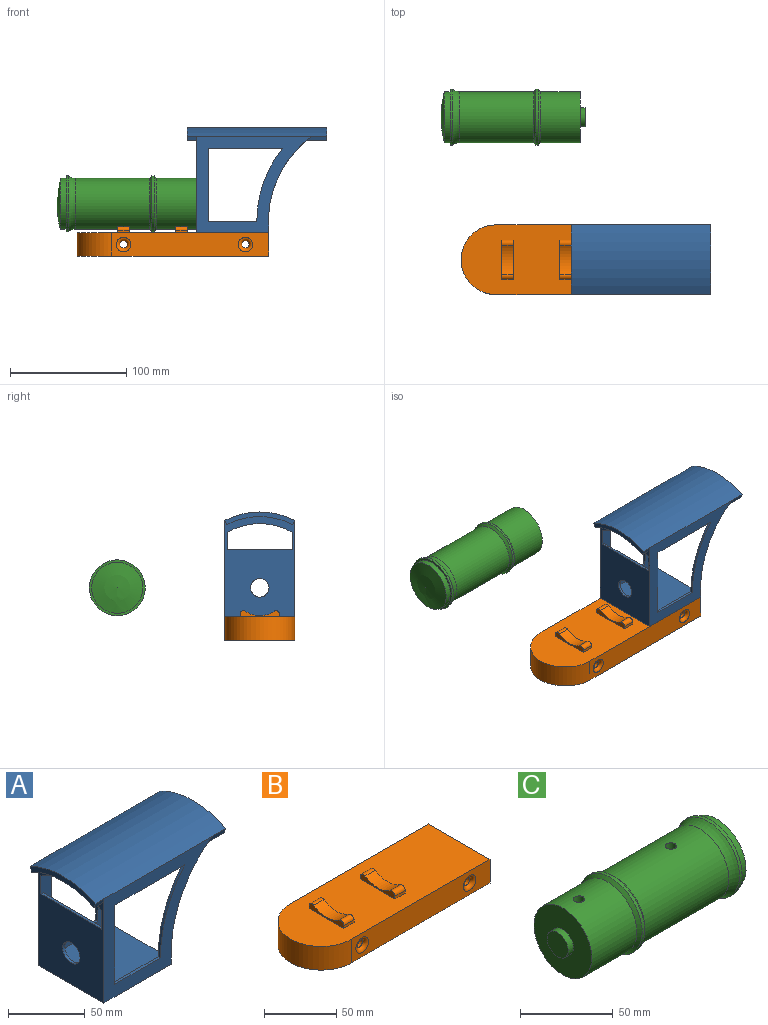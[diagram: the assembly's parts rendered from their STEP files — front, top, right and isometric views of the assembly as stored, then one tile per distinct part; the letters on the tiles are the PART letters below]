
ASSEMBLY  parts=3 mates=2
PART A: 32 faces, bbox 120.4x60x90.3 mm
  f0: plane 94.86x75.53mm, normal (0,1,0), area 2165.2mm2, adj f3,f5,f6,f7,f8,f9,f10,f19
  f1: plane 94.86x75.53mm, normal (0,-1,0), area 2165.2mm2, adj f3,f4,f5,f15,f16,f17,f18,f19
  f2: cylinder r=61.3mm len=57.24mm, axis (-1,0,0), area 476.4mm2, adj f3,f26,f28,f29
  f3: plane 86.3x60mm, normal (-1,0,0), area 3719.7mm2, adj f0,f1,f2,f11,f12,f14,f19,f21
  f4: cylinder r=90mm len=79mm, axis (0,-1,0), area 174.3mm2, adj f1,f13,f14,f23,f24
  f5: plane 60.2x56mm, normal (0,0,1), area 3371.2mm2, adj f0,f1,f13,f20
  f6: cylinder r=90mm len=79mm, axis (0,-1,0), area 174.3mm2, adj f0,f11,f13,f22,f24
  f7: plane 42x2mm, normal (0,0,1), area 84mm2, adj f0,f8,f10,f11
  f8: plane 63x2mm, normal (1,0,0), area 126mm2, adj f0,f7,f9,f11
  f9: plane 64.34x2mm, normal (0,0,-1), area 128.7mm2, adj f0,f8,f10,f11
  f10: cylinder r=100mm len=63mm, axis (0,-1,0), area 136.3mm2, adj f0,f7,f9,f11
  f11: plane 99.36x83mm, normal (0,-1,0), area 2872.4mm2, adj f3,f6,f7,f8,f9,f10,f12,f13
  f12: plane 62.2x60mm, normal (0,0,-1), area 3732mm2, adj f3,f11,f13,f14
  f13: plane 60x4mm, normal (1,0,0), area 240mm2, adj f4,f5,f6,f11,f12,f14
  f14: plane 99.36x83mm, normal (0,1,0), area 2872.4mm2, adj f3,f4,f12,f13,f15,f16,f17,f18
  f15: plane 42x2mm, normal (0,0,1), area 84mm2, adj f1,f14,f16,f18
  f16: cylinder r=100mm len=63mm, axis (0,-1,0), area 136.3mm2, adj f1,f14,f15,f17
  f17: plane 64.34x2mm, normal (0,0,-1), area 128.7mm2, adj f1,f14,f16,f18
  f18: plane 63x2mm, normal (1,0,0), area 126mm2, adj f1,f14,f15,f17
  f19: plane 56x2mm, normal (0,0,1), area 112mm2, adj f0,f1,f3,f20
  f20: plane 56x54mm, normal (1,0,0), area 2822.9mm2, adj f0,f1,f5,f19,f21
  f21: cylinder r=8mm len=16mm, axis (1,0,0), area 100.5mm2, adj f3,f20
  f22: plane 17.89x3.79mm, normal (0,-0.94,-0.34), area 62.6mm2, adj f6,f24,f25,f27
  f23: plane 17.89x3.79mm, normal (0,0.94,-0.34), area 62.6mm2, adj f4,f24,f25,f27
  f24: cylinder r=61.3mm len=110.36mm, axis (-1,0,0), area 6442.9mm2, adj f0,f1,f4,f6,f22,f23,f25,f31
  f25: plane 60x11.09mm, normal (1,0,0), area 243.8mm2, adj f22,f23,f24,f27
  f26: plane 8x3.79mm, normal (0,0.94,-0.34), area 32.3mm2, adj f2,f3,f27,f29
  f27: cylinder r=65.3mm len=120.36mm, axis (-1,0,0), area 7503.3mm2, adj f11,f14,f22,f23,f25,f26,f28,f29
  f28: plane 8x3.79mm, normal (0,-0.94,-0.34), area 32.3mm2, adj f2,f3,f27,f29
  f29: plane 60x11.09mm, normal (-1,0,0), area 243.8mm2, adj f2,f26,f27,f28
  f30: cylinder r=55.3mm len=56mm, axis (-1,0,0), area 117.4mm2, adj f0,f1,f3,f31
  f31: plane 56x13.61mm, normal (1,0,0), area 350.5mm2, adj f0,f1,f24,f30
PART B: 30 faces, bbox 165x60x25.3 mm
  f0: plane 34x5.29mm, normal (1,0,0), area 99.6mm2, adj f1,f18,f19,f25,f26,f27
  f1: plane 165x60mm, normal (0,0,1), area 8833.7mm2, adj f0,f2,f3,f4,f5,f17,f18,f19
  f2: cylinder r=30mm len=60mm, axis (0,0,-1), area 1885mm2, adj f1,f3,f5,f6
  f3: plane 135x20mm, normal (0,-1,0), area 2454.6mm2, adj f1,f2,f4,f6,f11,f12
  f4: plane 60x20mm, normal (1,0,0), area 1193.7mm2, adj f1,f3,f5,f6,f13,f15
  f5: plane 135x20mm, normal (0,1,0), area 2454.6mm2, adj f1,f2,f4,f6,f9,f10
  f6: plane 165x60mm, normal (0,0,-1), area 9513.7mm2, adj f2,f3,f4,f5
  f7: cylinder r=3.25mm len=54mm, axis (0,-1,0), area 1102.7mm2, adj f10,f11
  f8: cylinder r=3.25mm len=54mm, axis (0,-1,0), area 1102.7mm2, adj f9,f12
  f9: torus R=6.25mm, axis (0,-1,0), area 128.5mm2, adj f5,f8
  f10: torus R=6.25mm, axis (0,-1,0), area 128.5mm2, adj f5,f7
  f11: torus R=6.25mm, axis (0,1,0), area 128.5mm2, adj f3,f7
  f12: torus R=6.25mm, axis (0,1,0), area 128.5mm2, adj f3,f8
  f13: cylinder r=1mm len=10mm, axis (1,0,0), area 62.8mm2, adj f4,f14
  f14: plane 2x2mm, normal (1,0,0), area 3.1mm2, adj f13
  f15: cylinder r=1mm len=10mm, axis (1,0,0), area 62.8mm2, adj f4,f16
  f16: plane 2x2mm, normal (1,0,0), area 3.1mm2, adj f15
  f17: plane 34x5.29mm, normal (-1,0,0), area 99.6mm2, adj f1,f18,f19,f25,f26,f27
  f18: plane 10x2.29mm, normal (0,-1,0), area 22.9mm2, adj f0,f1,f17,f26
  f19: plane 10x2.29mm, normal (0,1,0), area 22.9mm2, adj f0,f1,f17,f27
  f20: plane 34x5.29mm, normal (-1,0,0), area 99.6mm2, adj f1,f21,f23,f24,f28,f29
  f21: plane 10x2.29mm, normal (0,-1,0), area 22.9mm2, adj f1,f20,f22,f28
  f22: plane 34x5.29mm, normal (1,0,0), area 99.6mm2, adj f1,f21,f23,f24,f28,f29
  f23: plane 10x2.29mm, normal (0,1,0), area 22.9mm2, adj f1,f20,f22,f29
  f24: cylinder r=22mm len=24.64mm, axis (1,0,0), area 261.5mm2, adj f20,f22,f28,f29
  f25: cylinder r=22mm len=24.64mm, axis (1,0,0), area 261.5mm2, adj f0,f17,f26,f27
  f26: cylinder r=3mm len=10mm, axis (1,0,0), area 65mm2, adj f0,f17,f18,f25
  f27: cylinder r=3mm len=10mm, axis (1,0,0), area 65mm2, adj f0,f17,f19,f25
  f28: cylinder r=3mm len=10mm, axis (1,0,0), area 65mm2, adj f20,f21,f22,f24
  f29: cylinder r=3mm len=10mm, axis (1,0,0), area 65mm2, adj f20,f22,f23,f24
PART C: 17 faces, bbox 124x53.9x53.9 mm
  f0: cylinder r=22mm len=64mm, axis (-1,0,0), area 8818.4mm2, adj f2,f12,f15
  f1: cylinder r=22mm len=44mm, axis (-1,0,0), area 4708.8mm2, adj f4,f5,f13
  f2: cone r=22mm half-angle=45deg, axis (-1,0,0), area 408.7mm2, adj f0,f3
  f3: cylinder r=24mm len=48mm, axis (-1,0,0), area 301.6mm2, adj f2,f4
  f4: cone r=22mm half-angle=45deg, axis (1,0,0), area 408.7mm2, adj f1,f3
  f5: plane 44x44mm, normal (-1,0,0), area 1319.5mm2, adj f1,f6
  f6: cylinder r=8mm len=16mm, axis (-1,0,0), area 201.1mm2, adj f5,f7
  f7: plane 16x16mm, normal (-1,0,0), area 201.1mm2, adj f6
  f8: sphere r=90mm, area 1544mm2, adj f9
  f9: cylinder r=22mm len=44mm, axis (-1,0,0), area 691.2mm2, adj f8,f10
  f10: plane 48x48mm, normal (1,0,0), area 289mm2, adj f9,f11
  f11: cylinder r=24mm len=48mm, axis (-1,0,0), area 301.6mm2, adj f10,f12
  f12: torus R=32mm, axis (-1,0,0), area 916.8mm2, adj f0,f11
  f13: cylinder r=3mm len=12mm, axis (0,0,-1), area 224.3mm2, adj f1,f14
  f14: plane 6x6mm, normal (0,0,1), area 28.3mm2, adj f13
  f15: cylinder r=3mm len=12mm, axis (0,0,-1), area 224.3mm2, adj f0,f16
  f16: plane 6x6mm, normal (0,0,1), area 28.3mm2, adj f15
PLACE A t=(137.65,-50.72,85.16)mm
PLACE B t=(54.85,-20.72,55.16)mm
PLACE C rot(axis=(0,1,0),180deg) t=(131.65,101.99,100.16)mm
MATE planar C.f0 <-> A.f2  axis (1,0,0) through (127.65,101.99,100.16)mm
MATE planar B.f1 <-> A.f12  axis (0,0,1) through (189.85,-20.72,75.16)mm
